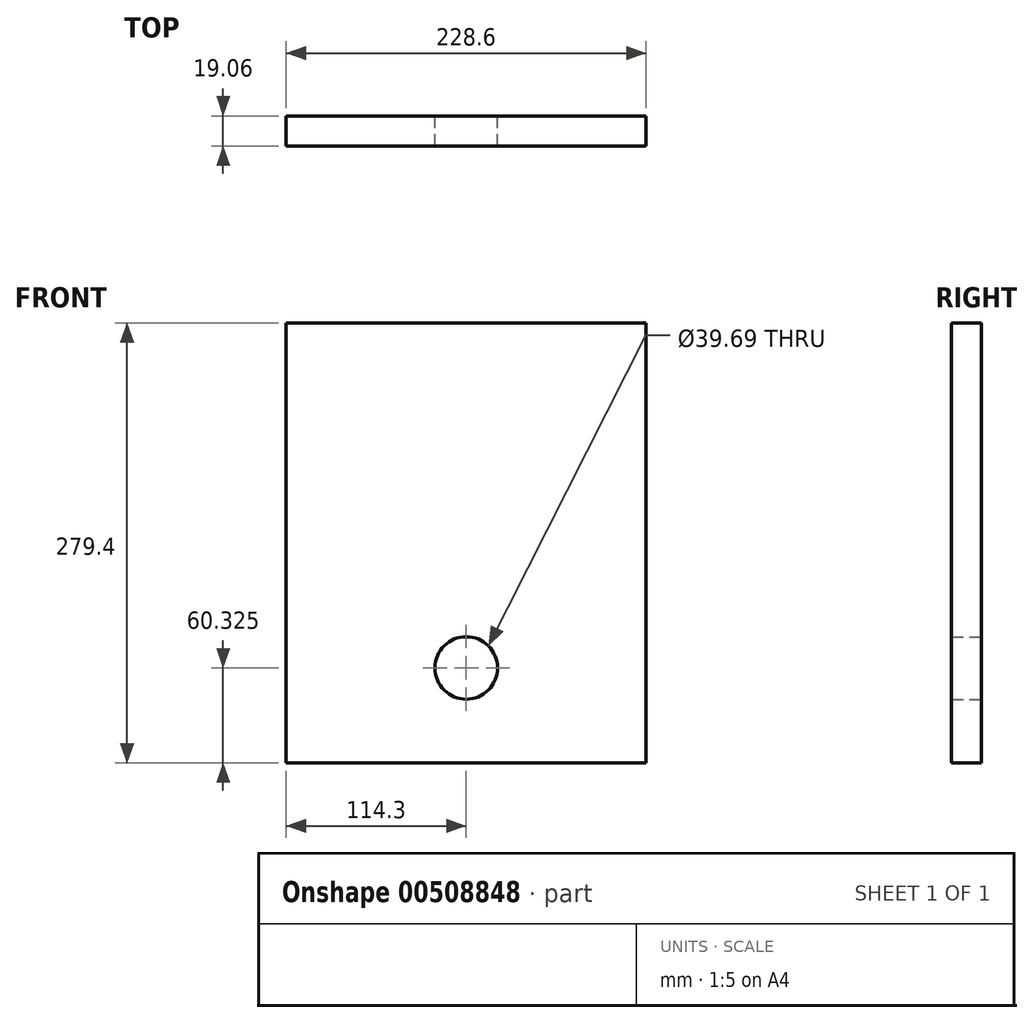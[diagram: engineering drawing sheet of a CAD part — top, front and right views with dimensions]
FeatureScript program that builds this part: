
annotation { "Feature Type Name" : "Feature", "Feature Type Description" : "" }
export const myFeature = defineFeature(function(context is Context, id is Id, definition is map)
    precondition{}
    {
        {
            var Q0;
            Q0=qCreatedBy(makeId("Front.planeOp"),FACE);
            var sketch = newSketch(context, id + "F0", { "sketchPlane" : qUnion([Q0])});
            skLineSegment(sketch, "E0.bottom", {"start": v(114.3, -139.7) * mm, "end": v(-114.3, -139.7) * mm});
            skLineSegment(sketch, "E0.top", {"start": v(114.3, 139.7) * mm, "end": v(-114.3, 139.7) * mm});
            skLineSegment(sketch, "E0.left", {"start": v(114.3, -139.7) * mm, "end": v(114.3, 139.7) * mm});
            skLineSegment(sketch, "E0.right", {"start": v(-114.3, -139.7) * mm, "end": v(-114.3, 139.7) * mm});
            skPoint(sketch, "E0.middle", {"position": v(0, 0) * mm});
            skCircle(sketch, "E1", {"center": v(0, -79.38) * mm, "radius": 19.84 * mm});
            skSolve(sketch);
        }
        {
            var Q0;
            Q0=makeQuery(id+"F0.imprint","IMPRINT",FACE,{"disambiguationData":[TD([[makeQuery(id+"F0.imprint","IMPRINT",EDGE,{"derivedFrom":sQuery(id+"F0.wireOp",EDGE,"E0.bottom")}),-1.0]])]});
            extrude(context, id + "F1", {"entities" : qUnion([Q0]), "endBound" : BoundingType.SYMMETRIC, "depth" : 19.05 * mm});
        }
    });
